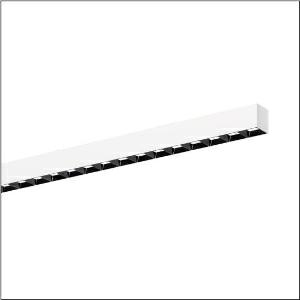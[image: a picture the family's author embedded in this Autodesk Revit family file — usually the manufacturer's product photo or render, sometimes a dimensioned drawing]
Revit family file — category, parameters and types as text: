
# Revit family: silica_21_51mx21dc3awb
name_source: partatom
category: Lighting Fixtures
units: mm (PartAtom-declared; Revit-internal decimal feet)

## family parameters
Cut with Voids When Loaded = No
Host = Face
Light Source = No
Part Type = Normal
Room Calculation Point = No
Round Connector Dimension = Use Diameter
Shared = No

## types (1)
- --- (1 x LED, 10800 lm, 69.3 W, 3000K)
    Apparent Load = 69 VA
    CIE Flux Codes = 87 99 100 100 100
    Color Rendering = 80
    Color Temperature = 3000K
    Default Elevation = 1800 mm
    Description = Silica 21, office luminaire, primary light control with darklight reflector, of PMMA, black, CAT 2 (L<= 3000cd/m²), light emission: direct distribution, primary light characteristic: symmetric, installation type: surface-mounted, LED, rated luminous flux: 10.800lm, luminous efficacy: 156lm/W, light colour: 830, colour temperature: 3000K, control gear: DALI 2, with terminal, 3+2-pole, max. 2.5mm², mains connection: 220..240V, AC, 50/60Hz, luminaire housing, of aluminium, traffic white (RAL 9016), length: 3.004mm, width: 53mm, height: 53mm, protection rating (complete): IP20, insulation class (complete): insulation class I (protective earthing), certification: CE, permissible operating ambient temperature: 0..+35°C, standard: EN 50419, packaging unit: 1 piece
    Height = 53 mm
    Lamp = 1 x LED
    Lamp Light Flux = 10800 lm
    Lamp Power = 69.3 W
    Lamp count = 1
    Length = 3004 mm
    Luminous efficacy = 156 lm/W
    Manufacturer = Siteco
    ModVariant = No
    Model = 51MX21DC3AWB
    Mounting Place = Ceiling
    Mounting Type = Surface mounted
    Number of Poles = 1
    OnlyDefault = Yes
    Power Factor = 1
    Product Name = Silica 21
    Product group = office luminaire | ceiling mounted
    ProductGroupID = 301
    Protection Class = Protection class I
    Protection Degree = IP 20
    RLX_Detail_Level = 1
    RLX_Emergency_Light_Flux = 0 lm
    RLX_Emergency_Type = 0
    RLX_Emergency_Type_DB = No
    RlxData = <blob elided: 62293 chars, md5=81d62be4>
    Socket = socket
    Standby Power = 0 W
    System Light Flux = 10800 lm
    System Power = 69 W
    Type Comments = factory setting: luminous flux: 100 % | dim-lin: 254 | 393 mA
    Type Image = l_1335873.jpg
    URL = http://relux.com
    VarID = @adj_125555
    Voltage = 0 V
    Weight = 0.00 kg
    Width = 53 mm

## geometry (parser evidence)
native form markers: Blend x4, Sweep x10
no freeform markers — native parametric forms only
